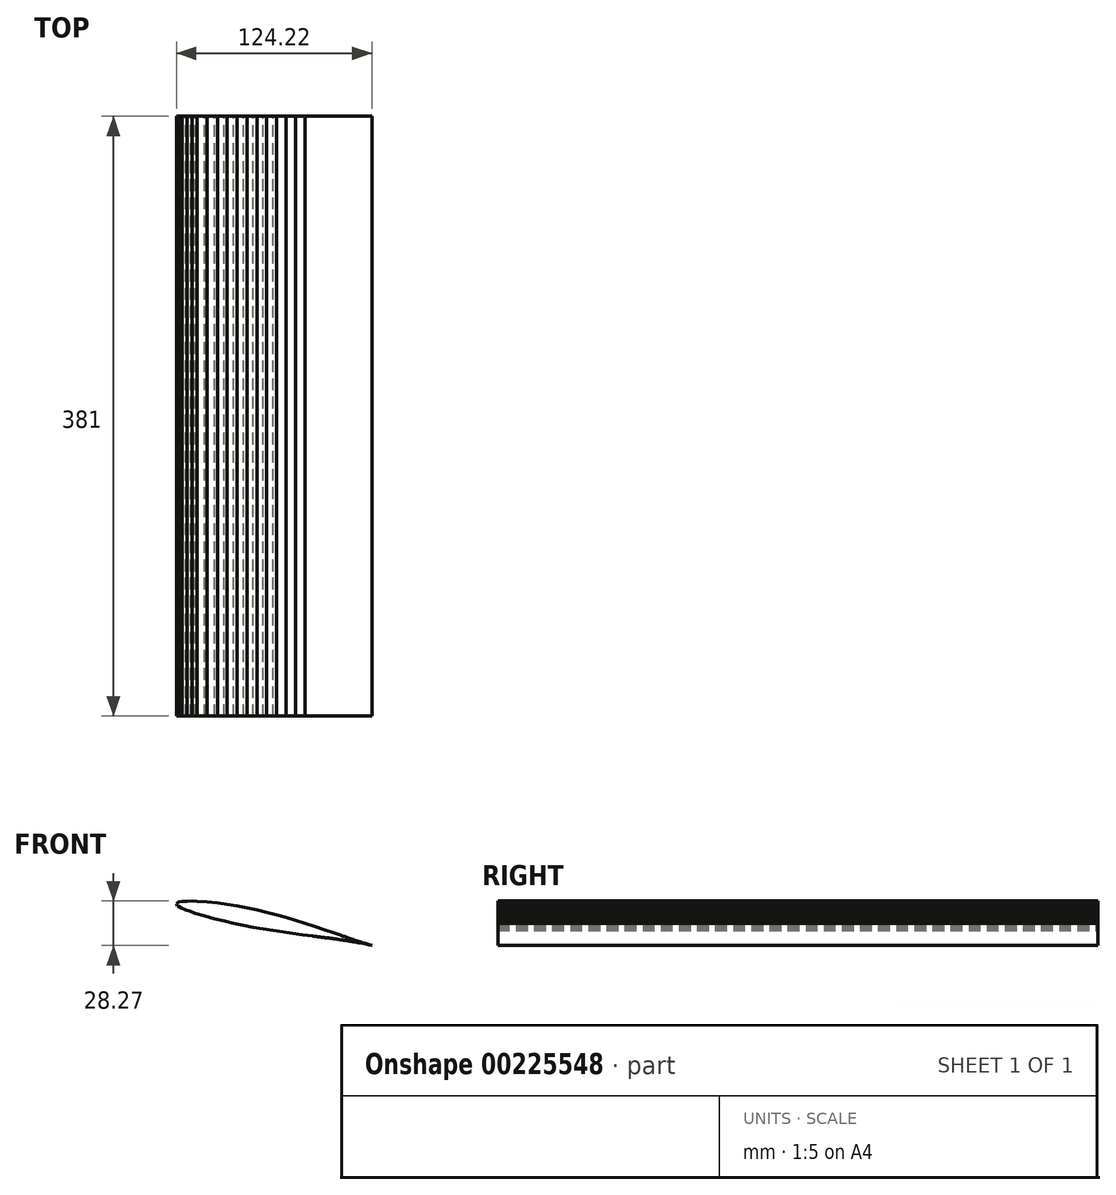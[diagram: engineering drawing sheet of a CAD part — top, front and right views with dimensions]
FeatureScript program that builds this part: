
annotation { "Feature Type Name" : "Feature", "Feature Type Description" : "" }
export const myFeature = defineFeature(function(context is Context, id is Id, definition is map)
    precondition{}
    {
        {
            var Q0;
            Q0=qCreatedBy(makeId("Front.planeOp"),FACE);
            var sketch = newSketch(context, id + "F0", { "sketchPlane" : qUnion([Q0])});
            skLineSegment(sketch, "E0", {"start": v(12.68, -0.26) * mm, "end": v(12.23, -0.21) * mm});
            skLineSegment(sketch, "E1", {"start": v(12.23, -0.21) * mm, "end": v(11.84, -0.17) * mm});
            skLineSegment(sketch, "E2", {"start": v(11.84, -0.17) * mm, "end": v(11.5, -0.14) * mm});
            skLineSegment(sketch, "E3", {"start": v(11.5, -0.14) * mm, "end": v(11.19, -0.1) * mm});
            skLineSegment(sketch, "E4", {"start": v(11.19, -0.1) * mm, "end": v(10.92, -0.07) * mm});
            skLineSegment(sketch, "E5", {"start": v(10.92, -0.07) * mm, "end": v(10.67, -0.05) * mm});
            skLineSegment(sketch, "E6", {"start": v(10.67, -0.05) * mm, "end": v(10.45, -0.02) * mm});
            skLineSegment(sketch, "E7", {"start": v(10.45, -0.02) * mm, "end": v(10.25, 0) * mm});
            skLineSegment(sketch, "E8", {"start": v(10.25, 0) * mm, "end": v(10.06, 0.02) * mm});
            skLineSegment(sketch, "E9", {"start": v(10.06, 0.02) * mm, "end": v(9.87, 0.04) * mm});
            skLineSegment(sketch, "E10", {"start": v(9.87, 0.04) * mm, "end": v(9.7, 0.06) * mm});
            skLineSegment(sketch, "E11", {"start": v(9.7, 0.06) * mm, "end": v(9.52, 0.08) * mm});
            skLineSegment(sketch, "E12", {"start": v(9.52, 0.08) * mm, "end": v(9.36, 0.1) * mm});
            skLineSegment(sketch, "E13", {"start": v(9.36, 0.1) * mm, "end": v(9.2, 0.12) * mm});
            skLineSegment(sketch, "E14", {"start": v(9.2, 0.12) * mm, "end": v(9.03, 0.14) * mm});
            skLineSegment(sketch, "E15", {"start": v(9.03, 0.14) * mm, "end": v(8.88, 0.16) * mm});
            skLineSegment(sketch, "E16", {"start": v(8.88, 0.16) * mm, "end": v(8.72, 0.18) * mm});
            skLineSegment(sketch, "E17", {"start": v(8.72, 0.18) * mm, "end": v(8.56, 0.2) * mm});
            skLineSegment(sketch, "E18", {"start": v(8.56, 0.2) * mm, "end": v(8.4, 0.22) * mm});
            skLineSegment(sketch, "E19", {"start": v(8.4, 0.22) * mm, "end": v(8.24, 0.24) * mm});
            skLineSegment(sketch, "E20", {"start": v(8.24, 0.24) * mm, "end": v(8.08, 0.26) * mm});
            skLineSegment(sketch, "E21", {"start": v(8.08, 0.26) * mm, "end": v(7.92, 0.28) * mm});
            skLineSegment(sketch, "E22", {"start": v(7.92, 0.28) * mm, "end": v(7.77, 0.3) * mm});
            skLineSegment(sketch, "E23", {"start": v(7.77, 0.3) * mm, "end": v(7.6, 0.31) * mm});
            skLineSegment(sketch, "E24", {"start": v(7.6, 0.31) * mm, "end": v(7.45, 0.33) * mm});
            skLineSegment(sketch, "E25", {"start": v(7.45, 0.33) * mm, "end": v(7.29, 0.35) * mm});
            skLineSegment(sketch, "E26", {"start": v(7.29, 0.35) * mm, "end": v(7.13, 0.37) * mm});
            skLineSegment(sketch, "E27", {"start": v(7.13, 0.37) * mm, "end": v(6.97, 0.4) * mm});
            skLineSegment(sketch, "E28", {"start": v(6.97, 0.4) * mm, "end": v(6.81, 0.4) * mm});
            skLineSegment(sketch, "E29", {"start": v(6.81, 0.4) * mm, "end": v(6.65, 0.43) * mm});
            skLineSegment(sketch, "E30", {"start": v(6.65, 0.43) * mm, "end": v(6.5, 0.45) * mm});
            skLineSegment(sketch, "E31", {"start": v(6.5, 0.45) * mm, "end": v(6.34, 0.46) * mm});
            skLineSegment(sketch, "E32", {"start": v(6.34, 0.46) * mm, "end": v(6.18, 0.48) * mm});
            skLineSegment(sketch, "E33", {"start": v(6.18, 0.48) * mm, "end": v(6.02, 0.5) * mm});
            skLineSegment(sketch, "E34", {"start": v(6.02, 0.5) * mm, "end": v(5.86, 0.52) * mm});
            skLineSegment(sketch, "E35", {"start": v(5.86, 0.52) * mm, "end": v(5.7, 0.54) * mm});
            skLineSegment(sketch, "E36", {"start": v(5.7, 0.54) * mm, "end": v(5.54, 0.56) * mm});
            skLineSegment(sketch, "E37", {"start": v(5.54, 0.56) * mm, "end": v(5.38, 0.57) * mm});
            skLineSegment(sketch, "E38", {"start": v(5.38, 0.57) * mm, "end": v(5.23, 0.6) * mm});
            skLineSegment(sketch, "E39", {"start": v(5.23, 0.6) * mm, "end": v(5.07, 0.6) * mm});
            skLineSegment(sketch, "E40", {"start": v(5.07, 0.6) * mm, "end": v(4.9, 0.63) * mm});
            skLineSegment(sketch, "E41", {"start": v(4.9, 0.63) * mm, "end": v(4.75, 0.64) * mm});
            skLineSegment(sketch, "E42", {"start": v(4.75, 0.64) * mm, "end": v(4.6, 0.66) * mm});
            skLineSegment(sketch, "E43", {"start": v(4.6, 0.66) * mm, "end": v(4.43, 0.68) * mm});
            skLineSegment(sketch, "E44", {"start": v(4.43, 0.68) * mm, "end": v(4.27, 0.7) * mm});
            skLineSegment(sketch, "E45", {"start": v(4.27, 0.7) * mm, "end": v(4.11, 0.71) * mm});
            skLineSegment(sketch, "E46", {"start": v(4.11, 0.71) * mm, "end": v(3.96, 0.73) * mm});
            skLineSegment(sketch, "E47", {"start": v(3.96, 0.73) * mm, "end": v(3.8, 0.74) * mm});
            skLineSegment(sketch, "E48", {"start": v(3.8, 0.74) * mm, "end": v(3.64, 0.76) * mm});
            skLineSegment(sketch, "E49", {"start": v(3.64, 0.76) * mm, "end": v(3.48, 0.77) * mm});
            skLineSegment(sketch, "E50", {"start": v(3.48, 0.77) * mm, "end": v(3.32, 0.79) * mm});
            skLineSegment(sketch, "E51", {"start": v(3.32, 0.79) * mm, "end": v(3.16, 0.8) * mm});
            skLineSegment(sketch, "E52", {"start": v(3.16, 0.8) * mm, "end": v(3, 0.82) * mm});
            skLineSegment(sketch, "E53", {"start": v(3, 0.82) * mm, "end": v(2.84, 0.83) * mm});
            skLineSegment(sketch, "E54", {"start": v(2.84, 0.83) * mm, "end": v(2.68, 0.85) * mm});
            skLineSegment(sketch, "E55", {"start": v(2.68, 0.85) * mm, "end": v(2.52, 0.86) * mm});
            skLineSegment(sketch, "E56", {"start": v(2.52, 0.86) * mm, "end": v(2.37, 0.88) * mm});
            skLineSegment(sketch, "E57", {"start": v(2.37, 0.88) * mm, "end": v(2.2, 0.89) * mm});
            skLineSegment(sketch, "E58", {"start": v(2.2, 0.89) * mm, "end": v(2.05, 0.9) * mm});
            skLineSegment(sketch, "E59", {"start": v(2.05, 0.9) * mm, "end": v(1.89, 0.91) * mm});
            skLineSegment(sketch, "E60", {"start": v(1.89, 0.91) * mm, "end": v(1.73, 0.93) * mm});
            skLineSegment(sketch, "E61", {"start": v(1.73, 0.93) * mm, "end": v(1.57, 0.94) * mm});
            skLineSegment(sketch, "E62", {"start": v(1.57, 0.94) * mm, "end": v(1.41, 0.95) * mm});
            skLineSegment(sketch, "E63", {"start": v(1.41, 0.95) * mm, "end": v(1.25, 0.96) * mm});
            skLineSegment(sketch, "E64", {"start": v(1.25, 0.96) * mm, "end": v(1.1, 0.98) * mm});
            skLineSegment(sketch, "E65", {"start": v(1.1, 0.98) * mm, "end": v(0.93, 0.99) * mm});
            skLineSegment(sketch, "E66", {"start": v(0.93, 0.99) * mm, "end": v(0.77, 1) * mm});
            skLineSegment(sketch, "E67", {"start": v(0.77, 1) * mm, "end": v(0.62, 1) * mm});
            skLineSegment(sketch, "E68", {"start": v(0.62, 1) * mm, "end": v(0.46, 1.02) * mm});
            skLineSegment(sketch, "E69", {"start": v(0.46, 1.02) * mm, "end": v(0.3, 1.03) * mm});
            skLineSegment(sketch, "E70", {"start": v(0.3, 1.03) * mm, "end": v(0.14, 1.04) * mm});
            skLineSegment(sketch, "E71", {"start": v(0.14, 1.04) * mm, "end": v(-0.02, 1.05) * mm});
            skLineSegment(sketch, "E72", {"start": v(-0.02, 1.05) * mm, "end": v(-0.18, 1.05) * mm});
            skLineSegment(sketch, "E73", {"start": v(-0.18, 1.05) * mm, "end": v(-0.34, 1.06) * mm});
            skLineSegment(sketch, "E74", {"start": v(-0.34, 1.06) * mm, "end": v(-0.5, 1.07) * mm});
            skLineSegment(sketch, "E75", {"start": v(-0.5, 1.07) * mm, "end": v(-0.66, 1.08) * mm});
            skLineSegment(sketch, "E76", {"start": v(-0.66, 1.08) * mm, "end": v(-0.82, 1.09) * mm});
            skLineSegment(sketch, "E77", {"start": v(-0.82, 1.09) * mm, "end": v(-0.98, 1.1) * mm});
            skLineSegment(sketch, "E78", {"start": v(-0.98, 1.1) * mm, "end": v(-1.14, 1.1) * mm});
            skLineSegment(sketch, "E79", {"start": v(-1.14, 1.1) * mm, "end": v(-1.3, 1.1) * mm});
            skLineSegment(sketch, "E80", {"start": v(-1.3, 1.1) * mm, "end": v(-1.45, 1.1) * mm});
            skLineSegment(sketch, "E81", {"start": v(-1.45, 1.1) * mm, "end": v(-1.61, 1.11) * mm});
            skLineSegment(sketch, "E82", {"start": v(-1.61, 1.11) * mm, "end": v(-1.77, 1.12) * mm});
            skLineSegment(sketch, "E83", {"start": v(-1.77, 1.12) * mm, "end": v(-1.93, 1.12) * mm});
            skLineSegment(sketch, "E84", {"start": v(-1.93, 1.12) * mm, "end": v(-2.1, 1.13) * mm});
            skLineSegment(sketch, "E85", {"start": v(-2.1, 1.13) * mm, "end": v(-2.25, 1.13) * mm});
            skLineSegment(sketch, "E86", {"start": v(-2.25, 1.13) * mm, "end": v(-2.4, 1.13) * mm});
            skLineSegment(sketch, "E87", {"start": v(-2.4, 1.13) * mm, "end": v(-2.57, 1.14) * mm});
            skLineSegment(sketch, "E88", {"start": v(-2.57, 1.14) * mm, "end": v(-2.73, 1.14) * mm});
            skLineSegment(sketch, "E89", {"start": v(-2.73, 1.14) * mm, "end": v(-2.89, 1.14) * mm});
            skLineSegment(sketch, "E90", {"start": v(-2.89, 1.14) * mm, "end": v(-3.05, 1.14) * mm});
            skLineSegment(sketch, "E91", {"start": v(-3.05, 1.14) * mm, "end": v(-3.2, 1.14) * mm});
            skLineSegment(sketch, "E92", {"start": v(-3.2, 1.14) * mm, "end": v(-3.36, 1.14) * mm});
            skLineSegment(sketch, "E93", {"start": v(-3.36, 1.14) * mm, "end": v(-3.52, 1.14) * mm});
            skLineSegment(sketch, "E94", {"start": v(-3.52, 1.14) * mm, "end": v(-3.68, 1.14) * mm});
            skLineSegment(sketch, "E95", {"start": v(-3.68, 1.14) * mm, "end": v(-3.84, 1.14) * mm});
            skLineSegment(sketch, "E96", {"start": v(-3.84, 1.14) * mm, "end": v(-4, 1.14) * mm});
            skLineSegment(sketch, "E97", {"start": v(-4, 1.14) * mm, "end": v(-4.16, 1.13) * mm});
            skLineSegment(sketch, "E98", {"start": v(-4.16, 1.13) * mm, "end": v(-4.32, 1.13) * mm});
            skLineSegment(sketch, "E99", {"start": v(-4.32, 1.13) * mm, "end": v(-4.48, 1.13) * mm});
            skLineSegment(sketch, "E100", {"start": v(-4.48, 1.13) * mm, "end": v(-4.64, 1.12) * mm});
            skLineSegment(sketch, "E101", {"start": v(-4.64, 1.12) * mm, "end": v(-4.8, 1.12) * mm});
            skLineSegment(sketch, "E102", {"start": v(-4.8, 1.12) * mm, "end": v(-4.96, 1.11) * mm});
            skLineSegment(sketch, "E103", {"start": v(-4.96, 1.11) * mm, "end": v(-5.12, 1.1) * mm});
            skLineSegment(sketch, "E104", {"start": v(-5.12, 1.1) * mm, "end": v(-5.28, 1.1) * mm});
            skLineSegment(sketch, "E105", {"start": v(-5.28, 1.1) * mm, "end": v(-5.43, 1.1) * mm});
            skLineSegment(sketch, "E106", {"start": v(-5.43, 1.1) * mm, "end": v(-5.6, 1.09) * mm});
            skLineSegment(sketch, "E107", {"start": v(-5.6, 1.09) * mm, "end": v(-5.75, 1.08) * mm});
            skLineSegment(sketch, "E108", {"start": v(-5.75, 1.08) * mm, "end": v(-5.91, 1.07) * mm});
            skLineSegment(sketch, "E109", {"start": v(-5.91, 1.07) * mm, "end": v(-6.07, 1.07) * mm});
            skLineSegment(sketch, "E110", {"start": v(-6.07, 1.07) * mm, "end": v(-6.23, 1.06) * mm});
            skLineSegment(sketch, "E111", {"start": v(-6.23, 1.06) * mm, "end": v(-6.4, 1.05) * mm});
            skLineSegment(sketch, "E112", {"start": v(-6.4, 1.05) * mm, "end": v(-6.55, 1.04) * mm});
            skLineSegment(sketch, "E113", {"start": v(-6.55, 1.04) * mm, "end": v(-6.7, 1.03) * mm});
            skLineSegment(sketch, "E114", {"start": v(-6.7, 1.03) * mm, "end": v(-6.87, 1.01) * mm});
            skLineSegment(sketch, "E115", {"start": v(-6.87, 1.01) * mm, "end": v(-7.03, 1) * mm});
            skLineSegment(sketch, "E116", {"start": v(-7.03, 1) * mm, "end": v(-7.19, 1) * mm});
            skLineSegment(sketch, "E117", {"start": v(-7.19, 1) * mm, "end": v(-7.35, 0.98) * mm});
            skLineSegment(sketch, "E118", {"start": v(-7.35, 0.98) * mm, "end": v(-7.5, 0.96) * mm});
            skLineSegment(sketch, "E119", {"start": v(-7.5, 0.96) * mm, "end": v(-7.66, 0.95) * mm});
            skLineSegment(sketch, "E120", {"start": v(-7.66, 0.95) * mm, "end": v(-7.82, 0.94) * mm});
            skLineSegment(sketch, "E121", {"start": v(-7.82, 0.94) * mm, "end": v(-7.98, 0.92) * mm});
            skLineSegment(sketch, "E122", {"start": v(-7.98, 0.92) * mm, "end": v(-8.14, 0.9) * mm});
            skLineSegment(sketch, "E123", {"start": v(-8.14, 0.9) * mm, "end": v(-8.3, 0.89) * mm});
            skLineSegment(sketch, "E124", {"start": v(-8.3, 0.89) * mm, "end": v(-8.46, 0.87) * mm});
            skLineSegment(sketch, "E125", {"start": v(-8.46, 0.87) * mm, "end": v(-8.62, 0.85) * mm});
            skLineSegment(sketch, "E126", {"start": v(-8.62, 0.85) * mm, "end": v(-8.78, 0.83) * mm});
            skLineSegment(sketch, "E127", {"start": v(-8.78, 0.83) * mm, "end": v(-8.94, 0.81) * mm});
            skLineSegment(sketch, "E128", {"start": v(-8.94, 0.81) * mm, "end": v(-9.1, 0.8) * mm});
            skLineSegment(sketch, "E129", {"start": v(-9.1, 0.8) * mm, "end": v(-9.25, 0.77) * mm});
            skLineSegment(sketch, "E130", {"start": v(-9.25, 0.77) * mm, "end": v(-9.4, 0.75) * mm});
            skLineSegment(sketch, "E131", {"start": v(-9.4, 0.75) * mm, "end": v(-9.56, 0.73) * mm});
            skLineSegment(sketch, "E132", {"start": v(-9.56, 0.73) * mm, "end": v(-9.7, 0.7) * mm});
            skLineSegment(sketch, "E133", {"start": v(-9.7, 0.7) * mm, "end": v(-9.85, 0.69) * mm});
            skLineSegment(sketch, "E134", {"start": v(-9.85, 0.69) * mm, "end": v(-9.98, 0.67) * mm});
            skLineSegment(sketch, "E135", {"start": v(-9.98, 0.67) * mm, "end": v(-10.1, 0.65) * mm});
            skLineSegment(sketch, "E136", {"start": v(-10.1, 0.65) * mm, "end": v(-10.22, 0.63) * mm});
            skLineSegment(sketch, "E137", {"start": v(-10.22, 0.63) * mm, "end": v(-10.32, 0.61) * mm});
            skLineSegment(sketch, "E138", {"start": v(-10.32, 0.61) * mm, "end": v(-10.42, 0.6) * mm});
            skLineSegment(sketch, "E139", {"start": v(-10.42, 0.6) * mm, "end": v(-10.51, 0.58) * mm});
            skLineSegment(sketch, "E140", {"start": v(-10.51, 0.58) * mm, "end": v(-10.6, 0.56) * mm});
            skLineSegment(sketch, "E141", {"start": v(-10.6, 0.56) * mm, "end": v(-10.68, 0.55) * mm});
            skLineSegment(sketch, "E142", {"start": v(-10.68, 0.55) * mm, "end": v(-10.76, 0.53) * mm});
            skLineSegment(sketch, "E143", {"start": v(-10.76, 0.53) * mm, "end": v(-10.84, 0.52) * mm});
            skLineSegment(sketch, "E144", {"start": v(-10.84, 0.52) * mm, "end": v(-10.92, 0.5) * mm});
            skLineSegment(sketch, "E145", {"start": v(-10.92, 0.5) * mm, "end": v(-11, 0.48) * mm});
            skLineSegment(sketch, "E146", {"start": v(-11, 0.48) * mm, "end": v(-11.08, 0.47) * mm});
            skLineSegment(sketch, "E147", {"start": v(-11.08, 0.47) * mm, "end": v(-11.16, 0.45) * mm});
            skLineSegment(sketch, "E148", {"start": v(-11.16, 0.45) * mm, "end": v(-11.24, 0.43) * mm});
            skLineSegment(sketch, "E149", {"start": v(-11.24, 0.43) * mm, "end": v(-11.32, 0.4) * mm});
            skLineSegment(sketch, "E150", {"start": v(-11.32, 0.4) * mm, "end": v(-11.4, 0.39) * mm});
            skLineSegment(sketch, "E151", {"start": v(-11.4, 0.39) * mm, "end": v(-11.48, 0.37) * mm});
            skLineSegment(sketch, "E152", {"start": v(-11.48, 0.37) * mm, "end": v(-11.56, 0.35) * mm});
            skLineSegment(sketch, "E153", {"start": v(-11.56, 0.35) * mm, "end": v(-11.63, 0.33) * mm});
            skLineSegment(sketch, "E154", {"start": v(-11.63, 0.33) * mm, "end": v(-11.71, 0.3) * mm});
            skLineSegment(sketch, "E155", {"start": v(-11.71, 0.3) * mm, "end": v(-11.79, 0.28) * mm});
            skLineSegment(sketch, "E156", {"start": v(-11.79, 0.28) * mm, "end": v(-11.86, 0.26) * mm});
            skLineSegment(sketch, "E157", {"start": v(-11.86, 0.26) * mm, "end": v(-11.93, 0.24) * mm});
            skLineSegment(sketch, "E158", {"start": v(-11.93, 0.24) * mm, "end": v(-12, 0.22) * mm});
            skLineSegment(sketch, "E159", {"start": v(-12, 0.22) * mm, "end": v(-12.06, 0.2) * mm});
            skLineSegment(sketch, "E160", {"start": v(-12.06, 0.2) * mm, "end": v(-12.11, 0.18) * mm});
            skLineSegment(sketch, "E161", {"start": v(-12.11, 0.18) * mm, "end": v(-12.17, 0.16) * mm});
            skLineSegment(sketch, "E162", {"start": v(-12.17, 0.16) * mm, "end": v(-12.21, 0.14) * mm});
            skLineSegment(sketch, "E163", {"start": v(-12.21, 0.14) * mm, "end": v(-12.26, 0.13) * mm});
            skLineSegment(sketch, "E164", {"start": v(-12.26, 0.13) * mm, "end": v(-12.3, 0.1) * mm});
            skLineSegment(sketch, "E165", {"start": v(-12.3, 0.1) * mm, "end": v(-12.33, 0.1) * mm});
            skLineSegment(sketch, "E166", {"start": v(-12.33, 0.1) * mm, "end": v(-12.36, 0.08) * mm});
            skLineSegment(sketch, "E167", {"start": v(-12.36, 0.08) * mm, "end": v(-12.4, 0.07) * mm});
            skLineSegment(sketch, "E168", {"start": v(-12.4, 0.07) * mm, "end": v(-12.42, 0.06) * mm});
            skLineSegment(sketch, "E169", {"start": v(-12.42, 0.06) * mm, "end": v(-12.44, 0.04) * mm});
            skLineSegment(sketch, "E170", {"start": v(-12.44, 0.04) * mm, "end": v(-12.46, 0.03) * mm});
            skLineSegment(sketch, "E171", {"start": v(-12.46, 0.03) * mm, "end": v(-12.48, 0.02) * mm});
            skLineSegment(sketch, "E172", {"start": v(-12.48, 0.02) * mm, "end": v(-12.5, 0.01) * mm});
            skLineSegment(sketch, "E173", {"start": v(-12.5, 0.01) * mm, "end": v(-12.51, 0) * mm});
            skLineSegment(sketch, "E174", {"start": v(-12.51, 0) * mm, "end": v(-12.53, 0) * mm});
            skLineSegment(sketch, "E175", {"start": v(-12.53, 0) * mm, "end": v(-12.54, 0) * mm});
            skLineSegment(sketch, "E176", {"start": v(-12.54, 0) * mm, "end": v(-12.55, -0.02) * mm});
            skLineSegment(sketch, "E177", {"start": v(-12.55, -0.02) * mm, "end": v(-12.56, -0.02) * mm});
            skLineSegment(sketch, "E178", {"start": v(-12.56, -0.02) * mm, "end": v(-12.57, -0.03) * mm});
            skLineSegment(sketch, "E179", {"start": v(-12.57, -0.03) * mm, "end": v(-12.58, -0.04) * mm});
            skLineSegment(sketch, "E180", {"start": v(-12.58, -0.04) * mm, "end": v(-12.59, -0.05) * mm});
            skLineSegment(sketch, "E181", {"start": v(-12.59, -0.05) * mm, "end": v(-12.6, -0.06) * mm});
            skLineSegment(sketch, "E182", {"start": v(-12.6, -0.06) * mm, "end": v(-12.6, -0.07) * mm});
            skLineSegment(sketch, "E183", {"start": v(-12.6, -0.07) * mm, "end": v(-12.62, -0.08) * mm});
            skLineSegment(sketch, "E184", {"start": v(-12.62, -0.08) * mm, "end": v(-12.63, -0.1) * mm});
            skLineSegment(sketch, "E185", {"start": v(-12.63, -0.1) * mm, "end": v(-12.64, -0.12) * mm});
            skLineSegment(sketch, "E186", {"start": v(-12.64, -0.12) * mm, "end": v(-12.65, -0.14) * mm});
            skLineSegment(sketch, "E187", {"start": v(-12.65, -0.14) * mm, "end": v(-12.66, -0.16) * mm});
            skLineSegment(sketch, "E188", {"start": v(-12.66, -0.16) * mm, "end": v(-12.67, -0.19) * mm});
            skLineSegment(sketch, "E189", {"start": v(-12.67, -0.19) * mm, "end": v(-12.68, -0.2) * mm});
            skLineSegment(sketch, "E190", {"start": v(-12.68, -0.2) * mm, "end": v(-12.68, -0.23) * mm});
            skLineSegment(sketch, "E191", {"start": v(-12.68, -0.23) * mm, "end": v(-12.68, -0.26) * mm});
            skLineSegment(sketch, "E192", {"start": v(-12.68, -0.26) * mm, "end": v(-12.67, -0.28) * mm});
            skLineSegment(sketch, "E193", {"start": v(-12.67, -0.28) * mm, "end": v(-12.67, -0.3) * mm});
            skLineSegment(sketch, "E194", {"start": v(-12.67, -0.3) * mm, "end": v(-12.66, -0.32) * mm});
            skLineSegment(sketch, "E195", {"start": v(-12.66, -0.32) * mm, "end": v(-12.65, -0.35) * mm});
            skLineSegment(sketch, "E196", {"start": v(-12.65, -0.35) * mm, "end": v(-12.63, -0.37) * mm});
            skLineSegment(sketch, "E197", {"start": v(-12.63, -0.37) * mm, "end": v(-12.62, -0.38) * mm});
            skLineSegment(sketch, "E198", {"start": v(-12.62, -0.38) * mm, "end": v(-12.6, -0.4) * mm});
            skLineSegment(sketch, "E199", {"start": v(-12.6, -0.4) * mm, "end": v(-12.6, -0.41) * mm});
            skLineSegment(sketch, "E200", {"start": v(-12.6, -0.41) * mm, "end": v(-12.58, -0.43) * mm});
            skLineSegment(sketch, "E201", {"start": v(-12.58, -0.43) * mm, "end": v(-12.57, -0.44) * mm});
            skLineSegment(sketch, "E202", {"start": v(-12.57, -0.44) * mm, "end": v(-12.56, -0.44) * mm});
            skLineSegment(sketch, "E203", {"start": v(-12.56, -0.44) * mm, "end": v(-12.55, -0.45) * mm});
            skLineSegment(sketch, "E204", {"start": v(-12.55, -0.45) * mm, "end": v(-12.54, -0.46) * mm});
            skLineSegment(sketch, "E205", {"start": v(-12.54, -0.46) * mm, "end": v(-12.52, -0.46) * mm});
            skLineSegment(sketch, "E206", {"start": v(-12.52, -0.46) * mm, "end": v(-12.51, -0.47) * mm});
            skLineSegment(sketch, "E207", {"start": v(-12.51, -0.47) * mm, "end": v(-12.5, -0.48) * mm});
            skLineSegment(sketch, "E208", {"start": v(-12.5, -0.48) * mm, "end": v(-12.49, -0.48) * mm});
            skLineSegment(sketch, "E209", {"start": v(-12.49, -0.48) * mm, "end": v(-12.48, -0.49) * mm});
            skLineSegment(sketch, "E210", {"start": v(-12.48, -0.49) * mm, "end": v(-12.46, -0.5) * mm});
            skLineSegment(sketch, "E211", {"start": v(-12.46, -0.5) * mm, "end": v(-12.44, -0.5) * mm});
            skLineSegment(sketch, "E212", {"start": v(-12.44, -0.5) * mm, "end": v(-12.42, -0.5) * mm});
            skLineSegment(sketch, "E213", {"start": v(-12.42, -0.5) * mm, "end": v(-12.4, -0.51) * mm});
            skLineSegment(sketch, "E214", {"start": v(-12.4, -0.51) * mm, "end": v(-12.38, -0.52) * mm});
            skLineSegment(sketch, "E215", {"start": v(-12.38, -0.52) * mm, "end": v(-12.35, -0.53) * mm});
            skLineSegment(sketch, "E216", {"start": v(-12.35, -0.53) * mm, "end": v(-12.32, -0.54) * mm});
            skLineSegment(sketch, "E217", {"start": v(-12.32, -0.54) * mm, "end": v(-12.29, -0.55) * mm});
            skLineSegment(sketch, "E218", {"start": v(-12.29, -0.55) * mm, "end": v(-12.25, -0.56) * mm});
            skLineSegment(sketch, "E219", {"start": v(-12.25, -0.56) * mm, "end": v(-12.21, -0.57) * mm});
            skLineSegment(sketch, "E220", {"start": v(-12.21, -0.57) * mm, "end": v(-12.17, -0.58) * mm});
            skLineSegment(sketch, "E221", {"start": v(-12.17, -0.58) * mm, "end": v(-12.12, -0.6) * mm});
            skLineSegment(sketch, "E222", {"start": v(-12.12, -0.6) * mm, "end": v(-12.07, -0.6) * mm});
            skLineSegment(sketch, "E223", {"start": v(-12.07, -0.6) * mm, "end": v(-12, -0.62) * mm});
            skLineSegment(sketch, "E224", {"start": v(-12, -0.62) * mm, "end": v(-11.95, -0.63) * mm});
            skLineSegment(sketch, "E225", {"start": v(-11.95, -0.63) * mm, "end": v(-11.88, -0.65) * mm});
            skLineSegment(sketch, "E226", {"start": v(-11.88, -0.65) * mm, "end": v(-11.81, -0.66) * mm});
            skLineSegment(sketch, "E227", {"start": v(-11.81, -0.66) * mm, "end": v(-11.74, -0.68) * mm});
            skLineSegment(sketch, "E228", {"start": v(-11.74, -0.68) * mm, "end": v(-11.66, -0.7) * mm});
            skLineSegment(sketch, "E229", {"start": v(-11.66, -0.7) * mm, "end": v(-11.58, -0.7) * mm});
            skLineSegment(sketch, "E230", {"start": v(-11.58, -0.7) * mm, "end": v(-11.5, -0.72) * mm});
            skLineSegment(sketch, "E231", {"start": v(-11.5, -0.72) * mm, "end": v(-11.43, -0.73) * mm});
            skLineSegment(sketch, "E232", {"start": v(-11.43, -0.73) * mm, "end": v(-11.35, -0.75) * mm});
            skLineSegment(sketch, "E233", {"start": v(-11.35, -0.75) * mm, "end": v(-11.27, -0.76) * mm});
            skLineSegment(sketch, "E234", {"start": v(-11.27, -0.76) * mm, "end": v(-11.19, -0.77) * mm});
            skLineSegment(sketch, "E235", {"start": v(-11.19, -0.77) * mm, "end": v(-11.1, -0.78) * mm});
            skLineSegment(sketch, "E236", {"start": v(-11.1, -0.78) * mm, "end": v(-11.03, -0.8) * mm});
            skLineSegment(sketch, "E237", {"start": v(-11.03, -0.8) * mm, "end": v(-10.95, -0.8) * mm});
            skLineSegment(sketch, "E238", {"start": v(-10.95, -0.8) * mm, "end": v(-10.87, -0.81) * mm});
            skLineSegment(sketch, "E239", {"start": v(-10.87, -0.81) * mm, "end": v(-10.79, -0.82) * mm});
            skLineSegment(sketch, "E240", {"start": v(-10.79, -0.82) * mm, "end": v(-10.7, -0.83) * mm});
            skLineSegment(sketch, "E241", {"start": v(-10.7, -0.83) * mm, "end": v(-10.63, -0.84) * mm});
            skLineSegment(sketch, "E242", {"start": v(-10.63, -0.84) * mm, "end": v(-10.55, -0.85) * mm});
            skLineSegment(sketch, "E243", {"start": v(-10.55, -0.85) * mm, "end": v(-10.46, -0.86) * mm});
            skLineSegment(sketch, "E244", {"start": v(-10.46, -0.86) * mm, "end": v(-10.37, -0.87) * mm});
            skLineSegment(sketch, "E245", {"start": v(-10.37, -0.87) * mm, "end": v(-10.27, -0.88) * mm});
            skLineSegment(sketch, "E246", {"start": v(-10.27, -0.88) * mm, "end": v(-10.16, -0.9) * mm});
            skLineSegment(sketch, "E247", {"start": v(-10.16, -0.9) * mm, "end": v(-10.05, -0.9) * mm});
            skLineSegment(sketch, "E248", {"start": v(-10.05, -0.9) * mm, "end": v(-9.92, -0.91) * mm});
            skLineSegment(sketch, "E249", {"start": v(-9.92, -0.91) * mm, "end": v(-9.8, -0.93) * mm});
            skLineSegment(sketch, "E250", {"start": v(-9.8, -0.93) * mm, "end": v(-9.65, -0.94) * mm});
            skLineSegment(sketch, "E251", {"start": v(-9.65, -0.94) * mm, "end": v(-9.5, -0.95) * mm});
            skLineSegment(sketch, "E252", {"start": v(-9.5, -0.95) * mm, "end": v(-9.36, -0.96) * mm});
            skLineSegment(sketch, "E253", {"start": v(-9.36, -0.96) * mm, "end": v(-9.2, -0.97) * mm});
            skLineSegment(sketch, "E254", {"start": v(-9.2, -0.97) * mm, "end": v(-9.04, -0.98) * mm});
            skLineSegment(sketch, "E255", {"start": v(-9.04, -0.98) * mm, "end": v(-8.89, -1) * mm});
            skLineSegment(sketch, "E256", {"start": v(-8.89, -1) * mm, "end": v(-8.73, -1) * mm});
            skLineSegment(sketch, "E257", {"start": v(-8.73, -1) * mm, "end": v(-8.57, -1.02) * mm});
            skLineSegment(sketch, "E258", {"start": v(-8.57, -1.02) * mm, "end": v(-8.41, -1.03) * mm});
            skLineSegment(sketch, "E259", {"start": v(-8.41, -1.03) * mm, "end": v(-8.25, -1.04) * mm});
            skLineSegment(sketch, "E260", {"start": v(-8.25, -1.04) * mm, "end": v(-8.1, -1.05) * mm});
            skLineSegment(sketch, "E261", {"start": v(-8.1, -1.05) * mm, "end": v(-7.94, -1.05) * mm});
            skLineSegment(sketch, "E262", {"start": v(-7.94, -1.05) * mm, "end": v(-7.78, -1.06) * mm});
            skLineSegment(sketch, "E263", {"start": v(-7.78, -1.06) * mm, "end": v(-7.62, -1.07) * mm});
            skLineSegment(sketch, "E264", {"start": v(-7.62, -1.07) * mm, "end": v(-7.46, -1.08) * mm});
            skLineSegment(sketch, "E265", {"start": v(-7.46, -1.08) * mm, "end": v(-7.3, -1.08) * mm});
            skLineSegment(sketch, "E266", {"start": v(-7.3, -1.08) * mm, "end": v(-7.14, -1.09) * mm});
            skLineSegment(sketch, "E267", {"start": v(-7.14, -1.09) * mm, "end": v(-6.99, -1.1) * mm});
            skLineSegment(sketch, "E268", {"start": v(-6.99, -1.1) * mm, "end": v(-6.83, -1.1) * mm});
            skLineSegment(sketch, "E269", {"start": v(-6.83, -1.1) * mm, "end": v(-6.67, -1.1) * mm});
            skLineSegment(sketch, "E270", {"start": v(-6.67, -1.1) * mm, "end": v(-6.51, -1.11) * mm});
            skLineSegment(sketch, "E271", {"start": v(-6.51, -1.11) * mm, "end": v(-6.35, -1.12) * mm});
            skLineSegment(sketch, "E272", {"start": v(-6.35, -1.12) * mm, "end": v(-6.2, -1.12) * mm});
            skLineSegment(sketch, "E273", {"start": v(-6.2, -1.12) * mm, "end": v(-6.04, -1.12) * mm});
            skLineSegment(sketch, "E274", {"start": v(-6.04, -1.12) * mm, "end": v(-5.88, -1.13) * mm});
            skLineSegment(sketch, "E275", {"start": v(-5.88, -1.13) * mm, "end": v(-5.72, -1.13) * mm});
            skLineSegment(sketch, "E276", {"start": v(-5.72, -1.13) * mm, "end": v(-5.56, -1.13) * mm});
            skLineSegment(sketch, "E277", {"start": v(-5.56, -1.13) * mm, "end": v(-5.4, -1.13) * mm});
            skLineSegment(sketch, "E278", {"start": v(-5.4, -1.13) * mm, "end": v(-5.24, -1.14) * mm});
            skLineSegment(sketch, "E279", {"start": v(-5.24, -1.14) * mm, "end": v(-5.09, -1.14) * mm});
            skLineSegment(sketch, "E280", {"start": v(-5.09, -1.14) * mm, "end": v(-4.93, -1.14) * mm});
            skLineSegment(sketch, "E281", {"start": v(-4.93, -1.14) * mm, "end": v(-4.77, -1.14) * mm});
            skLineSegment(sketch, "E282", {"start": v(-4.77, -1.14) * mm, "end": v(-4.61, -1.14) * mm});
            skLineSegment(sketch, "E283", {"start": v(-4.61, -1.14) * mm, "end": v(-4.45, -1.14) * mm});
            skLineSegment(sketch, "E284", {"start": v(-4.45, -1.14) * mm, "end": v(-4.3, -1.14) * mm});
            skLineSegment(sketch, "E285", {"start": v(-4.3, -1.14) * mm, "end": v(-4.14, -1.14) * mm});
            skLineSegment(sketch, "E286", {"start": v(-4.14, -1.14) * mm, "end": v(-3.98, -1.14) * mm});
            skLineSegment(sketch, "E287", {"start": v(-3.98, -1.14) * mm, "end": v(-3.82, -1.14) * mm});
            skLineSegment(sketch, "E288", {"start": v(-3.82, -1.14) * mm, "end": v(-3.66, -1.14) * mm});
            skLineSegment(sketch, "E289", {"start": v(-3.66, -1.14) * mm, "end": v(-3.5, -1.13) * mm});
            skLineSegment(sketch, "E290", {"start": v(-3.5, -1.13) * mm, "end": v(-3.35, -1.13) * mm});
            skLineSegment(sketch, "E291", {"start": v(-3.35, -1.13) * mm, "end": v(-3.19, -1.13) * mm});
            skLineSegment(sketch, "E292", {"start": v(-3.19, -1.13) * mm, "end": v(-3.03, -1.13) * mm});
            skLineSegment(sketch, "E293", {"start": v(-3.03, -1.13) * mm, "end": v(-2.87, -1.12) * mm});
            skLineSegment(sketch, "E294", {"start": v(-2.87, -1.12) * mm, "end": v(-2.71, -1.12) * mm});
            skLineSegment(sketch, "E295", {"start": v(-2.71, -1.12) * mm, "end": v(-2.55, -1.11) * mm});
            skLineSegment(sketch, "E296", {"start": v(-2.55, -1.11) * mm, "end": v(-2.4, -1.11) * mm});
            skLineSegment(sketch, "E297", {"start": v(-2.4, -1.11) * mm, "end": v(-2.24, -1.1) * mm});
            skLineSegment(sketch, "E298", {"start": v(-2.24, -1.1) * mm, "end": v(-2.08, -1.1) * mm});
            skLineSegment(sketch, "E299", {"start": v(-2.08, -1.1) * mm, "end": v(-1.92, -1.1) * mm});
            skLineSegment(sketch, "E300", {"start": v(-1.92, -1.1) * mm, "end": v(-1.76, -1.09) * mm});
            skLineSegment(sketch, "E301", {"start": v(-1.76, -1.09) * mm, "end": v(-1.6, -1.08) * mm});
            skLineSegment(sketch, "E302", {"start": v(-1.6, -1.08) * mm, "end": v(-1.45, -1.08) * mm});
            skLineSegment(sketch, "E303", {"start": v(-1.45, -1.08) * mm, "end": v(-1.29, -1.07) * mm});
            skLineSegment(sketch, "E304", {"start": v(-1.29, -1.07) * mm, "end": v(-1.13, -1.06) * mm});
            skLineSegment(sketch, "E305", {"start": v(-1.13, -1.06) * mm, "end": v(-0.97, -1.06) * mm});
            skLineSegment(sketch, "E306", {"start": v(-0.97, -1.06) * mm, "end": v(-0.81, -1.05) * mm});
            skLineSegment(sketch, "E307", {"start": v(-0.81, -1.05) * mm, "end": v(-0.65, -1.04) * mm});
            skLineSegment(sketch, "E308", {"start": v(-0.65, -1.04) * mm, "end": v(-0.5, -1.03) * mm});
            skLineSegment(sketch, "E309", {"start": v(-0.5, -1.03) * mm, "end": v(-0.34, -1.03) * mm});
            skLineSegment(sketch, "E310", {"start": v(-0.34, -1.03) * mm, "end": v(-0.18, -1.02) * mm});
            skLineSegment(sketch, "E311", {"start": v(-0.18, -1.02) * mm, "end": v(-0.02, -1) * mm});
            skLineSegment(sketch, "E312", {"start": v(-0.02, -1) * mm, "end": v(0.14, -1) * mm});
            skLineSegment(sketch, "E313", {"start": v(0.14, -1) * mm, "end": v(0.3, -1) * mm});
            skLineSegment(sketch, "E314", {"start": v(0.3, -1) * mm, "end": v(0.45, -0.98) * mm});
            skLineSegment(sketch, "E315", {"start": v(0.45, -0.98) * mm, "end": v(0.61, -0.97) * mm});
            skLineSegment(sketch, "E316", {"start": v(0.61, -0.97) * mm, "end": v(0.77, -0.96) * mm});
            skLineSegment(sketch, "E317", {"start": v(0.77, -0.96) * mm, "end": v(0.93, -0.95) * mm});
            skLineSegment(sketch, "E318", {"start": v(0.93, -0.95) * mm, "end": v(1.09, -0.94) * mm});
            skLineSegment(sketch, "E319", {"start": v(1.09, -0.94) * mm, "end": v(1.25, -0.93) * mm});
            skLineSegment(sketch, "E320", {"start": v(1.25, -0.93) * mm, "end": v(1.4, -0.92) * mm});
            skLineSegment(sketch, "E321", {"start": v(1.4, -0.92) * mm, "end": v(1.56, -0.9) * mm});
            skLineSegment(sketch, "E322", {"start": v(1.56, -0.9) * mm, "end": v(1.72, -0.9) * mm});
            skLineSegment(sketch, "E323", {"start": v(1.72, -0.9) * mm, "end": v(1.88, -0.89) * mm});
            skLineSegment(sketch, "E324", {"start": v(1.88, -0.89) * mm, "end": v(2.04, -0.88) * mm});
            skLineSegment(sketch, "E325", {"start": v(2.04, -0.88) * mm, "end": v(2.2, -0.86) * mm});
            skLineSegment(sketch, "E326", {"start": v(2.2, -0.86) * mm, "end": v(2.35, -0.85) * mm});
            skLineSegment(sketch, "E327", {"start": v(2.35, -0.85) * mm, "end": v(2.51, -0.84) * mm});
            skLineSegment(sketch, "E328", {"start": v(2.51, -0.84) * mm, "end": v(2.67, -0.83) * mm});
            skLineSegment(sketch, "E329", {"start": v(2.67, -0.83) * mm, "end": v(2.83, -0.82) * mm});
            skLineSegment(sketch, "E330", {"start": v(2.83, -0.82) * mm, "end": v(2.99, -0.8) * mm});
            skLineSegment(sketch, "E331", {"start": v(2.99, -0.8) * mm, "end": v(3.15, -0.8) * mm});
            skLineSegment(sketch, "E332", {"start": v(3.15, -0.8) * mm, "end": v(3.3, -0.78) * mm});
            skLineSegment(sketch, "E333", {"start": v(3.3, -0.78) * mm, "end": v(3.46, -0.77) * mm});
            skLineSegment(sketch, "E334", {"start": v(3.46, -0.77) * mm, "end": v(3.62, -0.75) * mm});
            skLineSegment(sketch, "E335", {"start": v(3.62, -0.75) * mm, "end": v(3.78, -0.74) * mm});
            skLineSegment(sketch, "E336", {"start": v(3.78, -0.74) * mm, "end": v(3.94, -0.73) * mm});
            skLineSegment(sketch, "E337", {"start": v(3.94, -0.73) * mm, "end": v(4.1, -0.72) * mm});
            skLineSegment(sketch, "E338", {"start": v(4.1, -0.72) * mm, "end": v(4.26, -0.7) * mm});
            skLineSegment(sketch, "E339", {"start": v(4.26, -0.7) * mm, "end": v(4.42, -0.7) * mm});
            skLineSegment(sketch, "E340", {"start": v(4.42, -0.7) * mm, "end": v(4.57, -0.68) * mm});
            skLineSegment(sketch, "E341", {"start": v(4.57, -0.68) * mm, "end": v(4.73, -0.66) * mm});
            skLineSegment(sketch, "E342", {"start": v(4.73, -0.66) * mm, "end": v(4.9, -0.65) * mm});
            skLineSegment(sketch, "E343", {"start": v(4.9, -0.65) * mm, "end": v(5.05, -0.64) * mm});
            skLineSegment(sketch, "E344", {"start": v(5.05, -0.64) * mm, "end": v(5.2, -0.62) * mm});
            skLineSegment(sketch, "E345", {"start": v(5.2, -0.62) * mm, "end": v(5.37, -0.61) * mm});
            skLineSegment(sketch, "E346", {"start": v(5.37, -0.61) * mm, "end": v(5.53, -0.6) * mm});
            skLineSegment(sketch, "E347", {"start": v(5.53, -0.6) * mm, "end": v(5.69, -0.59) * mm});
            skLineSegment(sketch, "E348", {"start": v(5.69, -0.59) * mm, "end": v(5.84, -0.57) * mm});
            skLineSegment(sketch, "E349", {"start": v(5.84, -0.57) * mm, "end": v(6, -0.56) * mm});
            skLineSegment(sketch, "E350", {"start": v(6, -0.56) * mm, "end": v(6.16, -0.55) * mm});
            skLineSegment(sketch, "E351", {"start": v(6.16, -0.55) * mm, "end": v(6.32, -0.53) * mm});
            skLineSegment(sketch, "E352", {"start": v(6.32, -0.53) * mm, "end": v(6.48, -0.52) * mm});
            skLineSegment(sketch, "E353", {"start": v(6.48, -0.52) * mm, "end": v(6.64, -0.5) * mm});
            skLineSegment(sketch, "E354", {"start": v(6.64, -0.5) * mm, "end": v(6.8, -0.5) * mm});
            skLineSegment(sketch, "E355", {"start": v(6.8, -0.5) * mm, "end": v(6.96, -0.48) * mm});
            skLineSegment(sketch, "E356", {"start": v(6.96, -0.48) * mm, "end": v(7.11, -0.47) * mm});
            skLineSegment(sketch, "E357", {"start": v(7.11, -0.47) * mm, "end": v(7.27, -0.46) * mm});
            skLineSegment(sketch, "E358", {"start": v(7.27, -0.46) * mm, "end": v(7.43, -0.45) * mm});
            skLineSegment(sketch, "E359", {"start": v(7.43, -0.45) * mm, "end": v(7.6, -0.43) * mm});
            skLineSegment(sketch, "E360", {"start": v(7.6, -0.43) * mm, "end": v(7.75, -0.42) * mm});
            skLineSegment(sketch, "E361", {"start": v(7.75, -0.42) * mm, "end": v(7.9, -0.41) * mm});
            skLineSegment(sketch, "E362", {"start": v(7.9, -0.41) * mm, "end": v(8.07, -0.4) * mm});
            skLineSegment(sketch, "E363", {"start": v(8.07, -0.4) * mm, "end": v(8.23, -0.39) * mm});
            skLineSegment(sketch, "E364", {"start": v(8.23, -0.39) * mm, "end": v(8.39, -0.38) * mm});
            skLineSegment(sketch, "E365", {"start": v(8.39, -0.38) * mm, "end": v(8.54, -0.37) * mm});
            skLineSegment(sketch, "E366", {"start": v(8.54, -0.37) * mm, "end": v(8.7, -0.35) * mm});
            skLineSegment(sketch, "E367", {"start": v(8.7, -0.35) * mm, "end": v(8.86, -0.34) * mm});
            skLineSegment(sketch, "E368", {"start": v(8.86, -0.34) * mm, "end": v(9.02, -0.33) * mm});
            skLineSegment(sketch, "E369", {"start": v(9.02, -0.33) * mm, "end": v(9.18, -0.32) * mm});
            skLineSegment(sketch, "E370", {"start": v(9.18, -0.32) * mm, "end": v(9.34, -0.32) * mm});
            skLineSegment(sketch, "E371", {"start": v(9.34, -0.32) * mm, "end": v(9.51, -0.3) * mm});
            skLineSegment(sketch, "E372", {"start": v(9.51, -0.3) * mm, "end": v(9.68, -0.3) * mm});
            skLineSegment(sketch, "E373", {"start": v(9.68, -0.3) * mm, "end": v(9.86, -0.29) * mm});
            skLineSegment(sketch, "E374", {"start": v(9.86, -0.29) * mm, "end": v(10.05, -0.28) * mm});
            skLineSegment(sketch, "E375", {"start": v(10.05, -0.28) * mm, "end": v(10.24, -0.27) * mm});
            skLineSegment(sketch, "E376", {"start": v(10.24, -0.27) * mm, "end": v(10.45, -0.26) * mm});
            skLineSegment(sketch, "E377", {"start": v(10.45, -0.26) * mm, "end": v(10.67, -0.26) * mm});
            skLineSegment(sketch, "E378", {"start": v(10.67, -0.26) * mm, "end": v(10.9, -0.25) * mm});
            skLineSegment(sketch, "E379", {"start": v(10.9, -0.25) * mm, "end": v(11.18, -0.25) * mm});
            skLineSegment(sketch, "E380", {"start": v(11.18, -0.25) * mm, "end": v(11.49, -0.25) * mm});
            skLineSegment(sketch, "E381", {"start": v(11.49, -0.25) * mm, "end": v(11.84, -0.25) * mm});
            skLineSegment(sketch, "E382", {"start": v(11.84, -0.25) * mm, "end": v(12.23, -0.25) * mm});
            skLineSegment(sketch, "E383", {"start": v(12.23, -0.25) * mm, "end": v(12.68, -0.26) * mm});
            skLineSegment(sketch, "E384", {"start": v(12.68, -0.26) * mm, "end": v(11.41, -0.13) * mm});
            skLineSegment(sketch, "E385", {"start": v(11.41, -0.13) * mm, "end": v(10.14, 0.01) * mm});
            skLineSegment(sketch, "E386", {"start": v(10.14, 0.01) * mm, "end": v(8.88, 0.16) * mm});
            skLineSegment(sketch, "E387", {"start": v(8.88, 0.16) * mm, "end": v(7.6, 0.32) * mm});
            skLineSegment(sketch, "E388", {"start": v(7.6, 0.32) * mm, "end": v(6.34, 0.47) * mm});
            skLineSegment(sketch, "E389", {"start": v(6.34, 0.47) * mm, "end": v(5.07, 0.61) * mm});
            skLineSegment(sketch, "E390", {"start": v(5.07, 0.61) * mm, "end": v(3.8, 0.74) * mm});
            skLineSegment(sketch, "E391", {"start": v(3.8, 0.74) * mm, "end": v(2.52, 0.86) * mm});
            skLineSegment(sketch, "E392", {"start": v(2.52, 0.86) * mm, "end": v(1.25, 0.97) * mm});
            skLineSegment(sketch, "E393", {"start": v(1.25, 0.97) * mm, "end": v(-0.02, 1.05) * mm});
            skLineSegment(sketch, "E394", {"start": v(-0.02, 1.05) * mm, "end": v(-1.3, 1.1) * mm});
            skLineSegment(sketch, "E395", {"start": v(-1.3, 1.1) * mm, "end": v(-2.57, 1.14) * mm});
            skLineSegment(sketch, "E396", {"start": v(-2.57, 1.14) * mm, "end": v(-3.84, 1.14) * mm});
            skLineSegment(sketch, "E397", {"start": v(-3.84, 1.14) * mm, "end": v(-5.12, 1.11) * mm});
            skLineSegment(sketch, "E398", {"start": v(-5.12, 1.11) * mm, "end": v(-6.4, 1.05) * mm});
            skLineSegment(sketch, "E399", {"start": v(-6.4, 1.05) * mm, "end": v(-7.66, 0.96) * mm});
            skLineSegment(sketch, "E400", {"start": v(-7.66, 0.96) * mm, "end": v(-8.94, 0.82) * mm});
            skLineSegment(sketch, "E401", {"start": v(-8.94, 0.82) * mm, "end": v(-10.2, 0.64) * mm});
            skLineSegment(sketch, "E402", {"start": v(-10.2, 0.64) * mm, "end": v(-10.84, 0.52) * mm});
            skLineSegment(sketch, "E403", {"start": v(-10.84, 0.52) * mm, "end": v(-11.48, 0.38) * mm});
            skLineSegment(sketch, "E404", {"start": v(-11.48, 0.38) * mm, "end": v(-12.1, 0.19) * mm});
            skLineSegment(sketch, "E405", {"start": v(-12.1, 0.19) * mm, "end": v(-12.42, 0.06) * mm});
            skLineSegment(sketch, "E406", {"start": v(-12.42, 0.06) * mm, "end": v(-12.55, -0.01) * mm});
            skLineSegment(sketch, "E407", {"start": v(-12.55, -0.01) * mm, "end": v(-12.61, -0.06) * mm});
            skLineSegment(sketch, "E408", {"start": v(-12.61, -0.06) * mm, "end": v(-12.72, -0.26) * mm});
            skLineSegment(sketch, "E409", {"start": v(-12.72, -0.26) * mm, "end": v(-12.58, -0.44) * mm});
            skLineSegment(sketch, "E410", {"start": v(-12.58, -0.44) * mm, "end": v(-12.51, -0.47) * mm});
            skLineSegment(sketch, "E411", {"start": v(-12.51, -0.47) * mm, "end": v(-12.38, -0.53) * mm});
            skLineSegment(sketch, "E412", {"start": v(-12.38, -0.53) * mm, "end": v(-12.06, -0.61) * mm});
            skLineSegment(sketch, "E413", {"start": v(-12.06, -0.61) * mm, "end": v(-11.42, -0.74) * mm});
            skLineSegment(sketch, "E414", {"start": v(-11.42, -0.74) * mm, "end": v(-10.79, -0.83) * mm});
            skLineSegment(sketch, "E415", {"start": v(-10.79, -0.83) * mm, "end": v(-10.15, -0.9) * mm});
            skLineSegment(sketch, "E416", {"start": v(-10.15, -0.9) * mm, "end": v(-8.89, -1) * mm});
            skLineSegment(sketch, "E417", {"start": v(-8.89, -1) * mm, "end": v(-7.62, -1.07) * mm});
            skLineSegment(sketch, "E418", {"start": v(-7.62, -1.07) * mm, "end": v(-6.35, -1.12) * mm});
            skLineSegment(sketch, "E419", {"start": v(-6.35, -1.12) * mm, "end": v(-5.09, -1.14) * mm});
            skLineSegment(sketch, "E420", {"start": v(-5.09, -1.14) * mm, "end": v(-3.82, -1.14) * mm});
            skLineSegment(sketch, "E421", {"start": v(-3.82, -1.14) * mm, "end": v(-2.55, -1.12) * mm});
            skLineSegment(sketch, "E422", {"start": v(-2.55, -1.12) * mm, "end": v(-1.29, -1.07) * mm});
            skLineSegment(sketch, "E423", {"start": v(-1.29, -1.07) * mm, "end": v(-0.02, -1.01) * mm});
            skLineSegment(sketch, "E424", {"start": v(-0.02, -1.01) * mm, "end": v(1.25, -0.93) * mm});
            skLineSegment(sketch, "E425", {"start": v(1.25, -0.93) * mm, "end": v(2.51, -0.84) * mm});
            skLineSegment(sketch, "E426", {"start": v(2.51, -0.84) * mm, "end": v(3.78, -0.74) * mm});
            skLineSegment(sketch, "E427", {"start": v(3.78, -0.74) * mm, "end": v(5.05, -0.64) * mm});
            skLineSegment(sketch, "E428", {"start": v(5.05, -0.64) * mm, "end": v(6.32, -0.53) * mm});
            skLineSegment(sketch, "E429", {"start": v(6.32, -0.53) * mm, "end": v(7.6, -0.43) * mm});
            skLineSegment(sketch, "E430", {"start": v(7.6, -0.43) * mm, "end": v(8.86, -0.34) * mm});
            skLineSegment(sketch, "E431", {"start": v(8.86, -0.34) * mm, "end": v(10.13, -0.27) * mm});
            skLineSegment(sketch, "E432", {"start": v(10.13, -0.27) * mm, "end": v(11.4, -0.23) * mm});
            skLineSegment(sketch, "E433", {"start": v(11.4, -0.23) * mm, "end": v(12.68, -0.26) * mm});
            skSolve(sketch);
        }
        {
            var Q0;
            {var subQ10=sQuery(id+"F0.wireOp",EDGE,"E20");Q0=makeQuery(id+"F0.imprint","IMPRINT",FACE,{"disambiguationData":[TD([[makeQuery(id+"F0.imprint","IMPRINT",EDGE,{"derivedFrom":subQ10}),1.0]])]});}
            var Q1;
            {var subQ0=sQuery(id+"F0.wireOp",EDGE,"E28");Q1=makeQuery(id+"F0.imprint","IMPRINT",FACE,{"disambiguationData":[TD([[makeQuery(id+"F0.imprint","IMPRINT",EDGE,{"derivedFrom":subQ0}),-1.0]])]});}
            var Q2;
            {var subQ0=sQuery(id+"F0.wireOp",EDGE,"E349");Q2=makeQuery(id+"F0.imprint","IMPRINT",FACE,{"disambiguationData":[TD([[makeQuery(id+"F0.imprint","IMPRINT",EDGE,{"derivedFrom":subQ0}),1.0]])]});}
            var Q3;
            Q3=makeQuery(id+"F0.imprint","IMPRINT",FACE,{"disambiguationData":[TD([[makeQuery(id+"F0.imprint","IMPRINT",EDGE,{"derivedFrom":sQuery(id+"F0.wireOp",EDGE,"E0")}),1.0]])]});
            var Q4;
            {var subQ0=sQuery(id+"F0.wireOp",EDGE,"E348");Q4=makeQuery(id+"F0.imprint","IMPRINT",FACE,{"disambiguationData":[TD([[makeQuery(id+"F0.imprint","IMPRINT",EDGE,{"derivedFrom":subQ0}),1.0]])]});}
            var Q5;
            {var subQ0=sQuery(id+"F0.wireOp",EDGE,"E27");Q5=makeQuery(id+"F0.imprint","IMPRINT",FACE,{"disambiguationData":[TD([[makeQuery(id+"F0.imprint","IMPRINT",EDGE,{"derivedFrom":subQ0}),-1.0]])]});}
            var Q6;
            {var subQ0=sQuery(id+"F0.wireOp",EDGE,"E22");Q6=makeQuery(id+"F0.imprint","IMPRINT",FACE,{"disambiguationData":[TD([[makeQuery(id+"F0.imprint","IMPRINT",EDGE,{"derivedFrom":subQ0}),-1.0]])]});}
            var Q7;
            {var subQ1=sQuery(id+"F0.wireOp",EDGE,"E14");Q7=makeQuery(id+"F0.imprint","IMPRINT",FACE,{"disambiguationData":[TD([[makeQuery(id+"F0.imprint","IMPRINT",EDGE,{"derivedFrom":subQ1}),1.0]])]});}
            var Q8;
            {var subQ0=sQuery(id+"F0.wireOp",EDGE,"E21");Q8=makeQuery(id+"F0.imprint","IMPRINT",FACE,{"disambiguationData":[TD([[makeQuery(id+"F0.imprint","IMPRINT",EDGE,{"derivedFrom":subQ0}),-1.0]])]});}
            extrude(context, id + "F1", {"entities" : qUnion([Q0, Q1, Q2, Q3, Q4, Q5, Q6, Q7, Q8]), "endBound" : BoundingType.SYMMETRIC, "depth" : 76.2 * mm});
        }
        {
            var Q0;
            Q0=makeQuery(id+"F1.opExtrude","SWEPT_BODY",BODY,{"disambiguationData":[OSD([sQuery(id+"F0.wireOp",EDGE,"E0"),sQuery(id+"F0.wireOp",EDGE,"E1"),sQuery(id+"F0.wireOp",EDGE,"E2"),sQuery(id+"F0.wireOp",EDGE,"E3"),sQuery(id+"F0.wireOp",EDGE,"E4"),sQuery(id+"F0.wireOp",EDGE,"E5"),sQuery(id+"F0.wireOp",EDGE,"E6"),sQuery(id+"F0.wireOp",EDGE,"E7"),sQuery(id+"F0.wireOp",EDGE,"E8"),sQuery(id+"F0.wireOp",EDGE,"E9"),sQuery(id+"F0.wireOp",EDGE,"E10"),sQuery(id+"F0.wireOp",EDGE,"E11"),sQuery(id+"F0.wireOp",EDGE,"E12"),sQuery(id+"F0.wireOp",EDGE,"E13"),sQuery(id+"F0.wireOp",EDGE,"E14"),sQuery(id+"F0.wireOp",EDGE,"E15"),sQuery(id+"F0.wireOp",EDGE,"E16"),sQuery(id+"F0.wireOp",EDGE,"E17"),sQuery(id+"F0.wireOp",EDGE,"E20"),sQuery(id+"F0.wireOp",EDGE,"E340"),sQuery(id+"F0.wireOp",EDGE,"E341"),sQuery(id+"F0.wireOp",EDGE,"E342"),sQuery(id+"F0.wireOp",EDGE,"E343"),sQuery(id+"F0.wireOp",EDGE,"E344"),sQuery(id+"F0.wireOp",EDGE,"E345"),sQuery(id+"F0.wireOp",EDGE,"E346"),sQuery(id+"F0.wireOp",EDGE,"E348"),sQuery(id+"F0.wireOp",EDGE,"E349"),sQuery(id+"F0.wireOp",EDGE,"E350"),sQuery(id+"F0.wireOp",EDGE,"E351"),sQuery(id+"F0.wireOp",EDGE,"E352"),sQuery(id+"F0.wireOp",EDGE,"E353"),sQuery(id+"F0.wireOp",EDGE,"E354"),sQuery(id+"F0.wireOp",EDGE,"E355"),sQuery(id+"F0.wireOp",EDGE,"E356"),sQuery(id+"F0.wireOp",EDGE,"E357"),sQuery(id+"F0.wireOp",EDGE,"E358"),sQuery(id+"F0.wireOp",EDGE,"E359"),sQuery(id+"F0.wireOp",EDGE,"E360"),sQuery(id+"F0.wireOp",EDGE,"E361"),sQuery(id+"F0.wireOp",EDGE,"E362"),sQuery(id+"F0.wireOp",EDGE,"E363"),sQuery(id+"F0.wireOp",EDGE,"E364"),sQuery(id+"F0.wireOp",EDGE,"E365"),sQuery(id+"F0.wireOp",EDGE,"E366"),sQuery(id+"F0.wireOp",EDGE,"E367"),sQuery(id+"F0.wireOp",EDGE,"E368"),sQuery(id+"F0.wireOp",EDGE,"E369"),sQuery(id+"F0.wireOp",EDGE,"E370"),sQuery(id+"F0.wireOp",EDGE,"E371"),sQuery(id+"F0.wireOp",EDGE,"E372"),sQuery(id+"F0.wireOp",EDGE,"E373"),sQuery(id+"F0.wireOp",EDGE,"E374"),sQuery(id+"F0.wireOp",EDGE,"E375"),sQuery(id+"F0.wireOp",EDGE,"E376"),sQuery(id+"F0.wireOp",EDGE,"E377"),sQuery(id+"F0.wireOp",EDGE,"E378"),sQuery(id+"F0.wireOp",EDGE,"E379"),sQuery(id+"F0.wireOp",EDGE,"E380"),sQuery(id+"F0.wireOp",EDGE,"E381"),sQuery(id+"F0.wireOp",EDGE,"E382"),sQuery(id+"F0.wireOp",EDGE,"E383"),sQuery(id+"F0.wireOp",EDGE,"E387"),sQuery(id+"F0.wireOp",EDGE,"E388"),sQuery(id+"F0.wireOp",EDGE,"E389"),sQuery(id+"F0.wireOp",EDGE,"E390"),sQuery(id+"F0.wireOp",EDGE,"E391"),sQuery(id+"F0.wireOp",EDGE,"E392"),sQuery(id+"F0.wireOp",EDGE,"E393"),sQuery(id+"F0.wireOp",EDGE,"E394"),sQuery(id+"F0.wireOp",EDGE,"E395"),sQuery(id+"F0.wireOp",EDGE,"E396"),sQuery(id+"F0.wireOp",EDGE,"E397"),sQuery(id+"F0.wireOp",EDGE,"E398"),sQuery(id+"F0.wireOp",EDGE,"E399"),sQuery(id+"F0.wireOp",EDGE,"E400"),sQuery(id+"F0.wireOp",EDGE,"E401"),sQuery(id+"F0.wireOp",EDGE,"E402"),sQuery(id+"F0.wireOp",EDGE,"E403"),sQuery(id+"F0.wireOp",EDGE,"E404"),sQuery(id+"F0.wireOp",EDGE,"E405"),sQuery(id+"F0.wireOp",EDGE,"E406"),sQuery(id+"F0.wireOp",EDGE,"E407"),sQuery(id+"F0.wireOp",EDGE,"E408"),sQuery(id+"F0.wireOp",EDGE,"E409"),sQuery(id+"F0.wireOp",EDGE,"E410"),sQuery(id+"F0.wireOp",EDGE,"E411"),sQuery(id+"F0.wireOp",EDGE,"E412"),sQuery(id+"F0.wireOp",EDGE,"E413"),sQuery(id+"F0.wireOp",EDGE,"E414"),sQuery(id+"F0.wireOp",EDGE,"E415"),sQuery(id+"F0.wireOp",EDGE,"E416"),sQuery(id+"F0.wireOp",EDGE,"E417"),sQuery(id+"F0.wireOp",EDGE,"E418"),sQuery(id+"F0.wireOp",EDGE,"E419"),sQuery(id+"F0.wireOp",EDGE,"E420"),sQuery(id+"F0.wireOp",EDGE,"E421"),sQuery(id+"F0.wireOp",EDGE,"E422"),sQuery(id+"F0.wireOp",EDGE,"E423"),sQuery(id+"F0.wireOp",EDGE,"E424"),sQuery(id+"F0.wireOp",EDGE,"E425"),sQuery(id+"F0.wireOp",EDGE,"E426"),sQuery(id+"F0.wireOp",EDGE,"E427"),sQuery(id+"F0.wireOp",EDGE,"E428")])]});
            var Q1;
            Q1=qCreatedBy(makeId("Origin.pointOp"),VERTEX);
            transform(context, id + "F2", {"entities" : qUnion([Q0]), "transformType" : TransformType.SCALE_UNIFORMLY, "scale" : 5, "scalePoint" : qUnion([Q1]), "makeCopy" : false});
        }
        {
            var Q0;
            Q0=makeQuery(id+"F1.opExtrude","SWEPT_BODY",BODY,{"disambiguationData":[OSD([sQuery(id+"F0.wireOp",EDGE,"E0"),sQuery(id+"F0.wireOp",EDGE,"E1"),sQuery(id+"F0.wireOp",EDGE,"E2"),sQuery(id+"F0.wireOp",EDGE,"E3"),sQuery(id+"F0.wireOp",EDGE,"E4"),sQuery(id+"F0.wireOp",EDGE,"E5"),sQuery(id+"F0.wireOp",EDGE,"E6"),sQuery(id+"F0.wireOp",EDGE,"E7"),sQuery(id+"F0.wireOp",EDGE,"E8"),sQuery(id+"F0.wireOp",EDGE,"E9"),sQuery(id+"F0.wireOp",EDGE,"E10"),sQuery(id+"F0.wireOp",EDGE,"E11"),sQuery(id+"F0.wireOp",EDGE,"E12"),sQuery(id+"F0.wireOp",EDGE,"E13"),sQuery(id+"F0.wireOp",EDGE,"E14"),sQuery(id+"F0.wireOp",EDGE,"E15"),sQuery(id+"F0.wireOp",EDGE,"E16"),sQuery(id+"F0.wireOp",EDGE,"E17"),sQuery(id+"F0.wireOp",EDGE,"E20"),sQuery(id+"F0.wireOp",EDGE,"E340"),sQuery(id+"F0.wireOp",EDGE,"E341"),sQuery(id+"F0.wireOp",EDGE,"E342"),sQuery(id+"F0.wireOp",EDGE,"E343"),sQuery(id+"F0.wireOp",EDGE,"E344"),sQuery(id+"F0.wireOp",EDGE,"E345"),sQuery(id+"F0.wireOp",EDGE,"E346"),sQuery(id+"F0.wireOp",EDGE,"E348"),sQuery(id+"F0.wireOp",EDGE,"E349"),sQuery(id+"F0.wireOp",EDGE,"E350"),sQuery(id+"F0.wireOp",EDGE,"E351"),sQuery(id+"F0.wireOp",EDGE,"E352"),sQuery(id+"F0.wireOp",EDGE,"E353"),sQuery(id+"F0.wireOp",EDGE,"E354"),sQuery(id+"F0.wireOp",EDGE,"E355"),sQuery(id+"F0.wireOp",EDGE,"E356"),sQuery(id+"F0.wireOp",EDGE,"E357"),sQuery(id+"F0.wireOp",EDGE,"E358"),sQuery(id+"F0.wireOp",EDGE,"E359"),sQuery(id+"F0.wireOp",EDGE,"E360"),sQuery(id+"F0.wireOp",EDGE,"E361"),sQuery(id+"F0.wireOp",EDGE,"E362"),sQuery(id+"F0.wireOp",EDGE,"E363"),sQuery(id+"F0.wireOp",EDGE,"E364"),sQuery(id+"F0.wireOp",EDGE,"E365"),sQuery(id+"F0.wireOp",EDGE,"E366"),sQuery(id+"F0.wireOp",EDGE,"E367"),sQuery(id+"F0.wireOp",EDGE,"E368"),sQuery(id+"F0.wireOp",EDGE,"E369"),sQuery(id+"F0.wireOp",EDGE,"E370"),sQuery(id+"F0.wireOp",EDGE,"E371"),sQuery(id+"F0.wireOp",EDGE,"E372"),sQuery(id+"F0.wireOp",EDGE,"E373"),sQuery(id+"F0.wireOp",EDGE,"E374"),sQuery(id+"F0.wireOp",EDGE,"E375"),sQuery(id+"F0.wireOp",EDGE,"E376"),sQuery(id+"F0.wireOp",EDGE,"E377"),sQuery(id+"F0.wireOp",EDGE,"E378"),sQuery(id+"F0.wireOp",EDGE,"E379"),sQuery(id+"F0.wireOp",EDGE,"E380"),sQuery(id+"F0.wireOp",EDGE,"E381"),sQuery(id+"F0.wireOp",EDGE,"E382"),sQuery(id+"F0.wireOp",EDGE,"E383"),sQuery(id+"F0.wireOp",EDGE,"E387"),sQuery(id+"F0.wireOp",EDGE,"E388"),sQuery(id+"F0.wireOp",EDGE,"E389"),sQuery(id+"F0.wireOp",EDGE,"E390"),sQuery(id+"F0.wireOp",EDGE,"E391"),sQuery(id+"F0.wireOp",EDGE,"E392"),sQuery(id+"F0.wireOp",EDGE,"E393"),sQuery(id+"F0.wireOp",EDGE,"E394"),sQuery(id+"F0.wireOp",EDGE,"E395"),sQuery(id+"F0.wireOp",EDGE,"E396"),sQuery(id+"F0.wireOp",EDGE,"E397"),sQuery(id+"F0.wireOp",EDGE,"E398"),sQuery(id+"F0.wireOp",EDGE,"E399"),sQuery(id+"F0.wireOp",EDGE,"E400"),sQuery(id+"F0.wireOp",EDGE,"E401"),sQuery(id+"F0.wireOp",EDGE,"E402"),sQuery(id+"F0.wireOp",EDGE,"E403"),sQuery(id+"F0.wireOp",EDGE,"E404"),sQuery(id+"F0.wireOp",EDGE,"E405"),sQuery(id+"F0.wireOp",EDGE,"E406"),sQuery(id+"F0.wireOp",EDGE,"E407"),sQuery(id+"F0.wireOp",EDGE,"E408"),sQuery(id+"F0.wireOp",EDGE,"E409"),sQuery(id+"F0.wireOp",EDGE,"E410"),sQuery(id+"F0.wireOp",EDGE,"E411"),sQuery(id+"F0.wireOp",EDGE,"E412"),sQuery(id+"F0.wireOp",EDGE,"E413"),sQuery(id+"F0.wireOp",EDGE,"E414"),sQuery(id+"F0.wireOp",EDGE,"E415"),sQuery(id+"F0.wireOp",EDGE,"E416"),sQuery(id+"F0.wireOp",EDGE,"E417"),sQuery(id+"F0.wireOp",EDGE,"E418"),sQuery(id+"F0.wireOp",EDGE,"E419"),sQuery(id+"F0.wireOp",EDGE,"E420"),sQuery(id+"F0.wireOp",EDGE,"E421"),sQuery(id+"F0.wireOp",EDGE,"E422"),sQuery(id+"F0.wireOp",EDGE,"E423"),sQuery(id+"F0.wireOp",EDGE,"E424"),sQuery(id+"F0.wireOp",EDGE,"E425"),sQuery(id+"F0.wireOp",EDGE,"E426"),sQuery(id+"F0.wireOp",EDGE,"E427"),sQuery(id+"F0.wireOp",EDGE,"E428")])]});
            var Q1;
            Q1=makeQuery(id+"F1.opExtrude","SWEPT_EDGE",EDGE,{"disambiguationData":[OSD([sQuery(id+"F0.wireOp",EDGE,"E394"),sQuery(id+"F0.wireOp",EDGE,"E395")])]});
            transform(context, id + "F3", {"entities" : qUnion([Q0]), "transformType" : TransformType.ROTATION, "transformAxis" : qUnion([Q1]), "angle" : 12 * degree, "makeCopy" : false});
        }
    });
